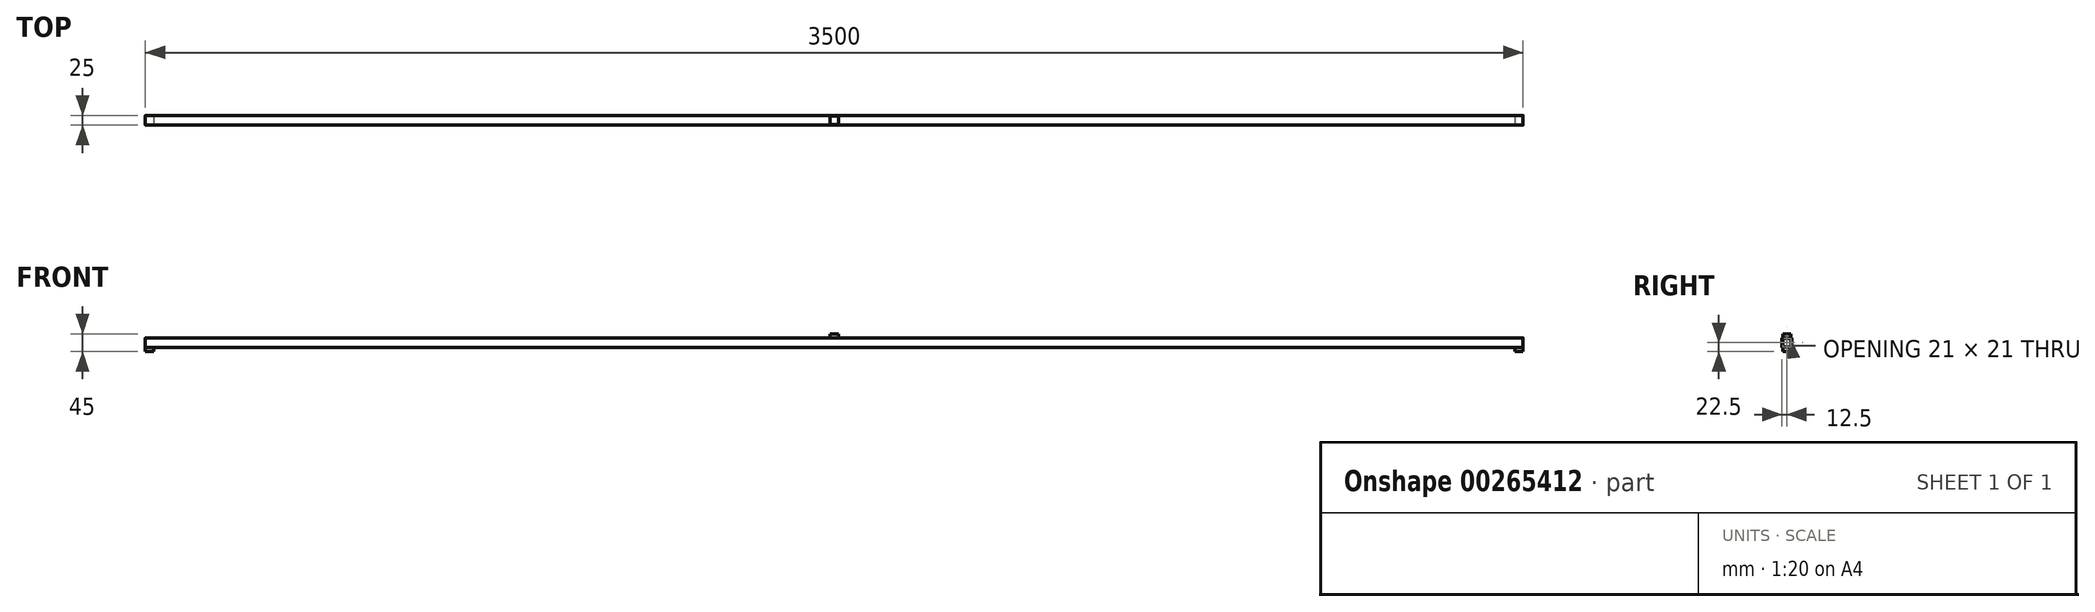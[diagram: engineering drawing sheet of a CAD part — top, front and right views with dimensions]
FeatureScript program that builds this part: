
annotation { "Feature Type Name" : "Feature", "Feature Type Description" : "" }
export const myFeature = defineFeature(function(context is Context, id is Id, definition is map)
    precondition{}
    {
        {
            var Q0;
            Q0=qCreatedBy(makeId("Right.planeOp"),FACE);
            var sketch = newSketch(context, id + "F0", { "sketchPlane" : qUnion([Q0])});
            skLineSegment(sketch, "E0.bottom", {"start": v(10.5, 12.5) * mm, "end": v(-10.5, 12.5) * mm});
            skLineSegment(sketch, "E0.top", {"start": v(10.5, -12.5) * mm, "end": v(-10.5, -12.5) * mm});
            skLineSegment(sketch, "E0.left", {"start": v(12.5, 10.5) * mm, "end": v(12.5, -10.5) * mm});
            skLineSegment(sketch, "E0.right", {"start": v(-12.5, 10.5) * mm, "end": v(-12.5, -10.5) * mm});
            skPoint(sketch, "E0.middle", {"position": v(0, 0) * mm});
            skLineSegment(sketch, "E1.bottom", {"start": v(8.5, 10.5) * mm, "end": v(-8.5, 10.5) * mm});
            skLineSegment(sketch, "E1.top", {"start": v(8.5, -10.5) * mm, "end": v(-8.5, -10.5) * mm});
            skLineSegment(sketch, "E1.left", {"start": v(10.5, 8.5) * mm, "end": v(10.5, -8.5) * mm});
            skLineSegment(sketch, "E1.right", {"start": v(-10.5, 8.5) * mm, "end": v(-10.5, -8.5) * mm});
            skPoint(sketch, "E2.visualSharp", {"position": v(12.5, 12.5) * mm});
            skArc(sketch, "E2.filletArc", {"start": v(12.5, 10.5) * mm, "mid": v(11.91, 11.91) * mm, "end": v(10.5, 12.5) * mm});
            skPoint(sketch, "E3.visualSharp", {"position": v(-12.5, 12.5) * mm});
            skArc(sketch, "E3.filletArc", {"start": v(-10.5, 12.5) * mm, "mid": v(-11.91, 11.91) * mm, "end": v(-12.5, 10.5) * mm});
            skArc(sketch, "E4.filletArc", {"start": v(-8.5, 10.5) * mm, "mid": v(-9.91, 9.91) * mm, "end": v(-10.5, 8.5) * mm});
            skArc(sketch, "E5.filletArc", {"start": v(10.5, 8.5) * mm, "mid": v(9.91, 9.91) * mm, "end": v(8.5, 10.5) * mm});
            skPoint(sketch, "E6.visualSharp", {"position": v(12.5, -12.5) * mm});
            skArc(sketch, "E6.filletArc", {"start": v(10.5, -12.5) * mm, "mid": v(11.91, -11.91) * mm, "end": v(12.5, -10.5) * mm});
            skArc(sketch, "E7.filletArc", {"start": v(8.5, -10.5) * mm, "mid": v(9.91, -9.91) * mm, "end": v(10.5, -8.5) * mm});
            skPoint(sketch, "E8.visualSharp", {"position": v(-10.5, -10.5) * mm});
            skArc(sketch, "E8.filletArc", {"start": v(-10.5, -8.5) * mm, "mid": v(-9.91, -9.91) * mm, "end": v(-8.5, -10.5) * mm});
            skPoint(sketch, "E9.visualSharp", {"position": v(-12.5, -12.5) * mm});
            skArc(sketch, "E9.filletArc", {"start": v(-12.5, -10.5) * mm, "mid": v(-11.91, -11.91) * mm, "end": v(-10.5, -12.5) * mm});
            skSolve(sketch);
        }
        {
            var Q0;
            Q0 = qSketchRegion(id + "F0", true);
            var Q1;
            Q1=makeQuery(id+"F0.imprint","IMPRINT",FACE,{"disambiguationData":[TD([[makeQuery(id+"F0.imprint","IMPRINT",EDGE,{"derivedFrom":sQuery(id+"F0.wireOp",EDGE,"E0.bottom")}),1.0]])]});
            extrude(context, id + "F1", {"entities" : qUnion([Q0, Q1]), "endBound" : BoundingType.SYMMETRIC, "depth" : 3500 * mm});
        }
        {
            var Q0;
            Q0=makeQuery(id+"F1.opExtrude","SWEPT_FACE",FACE,{"disambiguationData":[OSD([sQuery(id+"F0.wireOp",EDGE,"E0.bottom")])]});
            var sketch = newSketch(context, id + "F2", { "sketchPlane" : qUnion([Q0])});
            skLineSegment(sketch, "E10.bottom", {"start": v(10.46, 10.5) * mm, "end": v(-10.46, 10.5) * mm});
            skLineSegment(sketch, "E10.top", {"start": v(10.46, -10.5) * mm, "end": v(-10.46, -10.5) * mm});
            skLineSegment(sketch, "E10.left", {"start": v(10.46, 10.5) * mm, "end": v(10.46, -10.5) * mm});
            skLineSegment(sketch, "E10.right", {"start": v(-10.46, 10.5) * mm, "end": v(-10.46, -10.5) * mm});
            skPoint(sketch, "E10.middle", {"position": v(0, 0) * mm});
            skSolve(sketch);
        }
        {
            var Q0;
            Q0 = qSketchRegion(id + "F2", true);
            extrude(context, id + "F3", {"entities" : qUnion([Q0]), "operationType" : NewBodyOperationType.ADD, "depth" : 10 * mm});
        }
        {
            var Q0;
            Q0=makeQuery(id+"F1.opExtrude","SWEPT_FACE",FACE,{"disambiguationData":[OSD([sQuery(id+"F0.wireOp",EDGE,"E0.top")])]});
            var sketch = newSketch(context, id + "F4", { "sketchPlane" : qUnion([Q0])});
            skLineSegment(sketch, "E11.bottom", {"start": v(-1750, -10.5) * mm, "end": v(-1728.66, -10.5) * mm});
            skLineSegment(sketch, "E11.top", {"start": v(-1750, 10.5) * mm, "end": v(-1728.66, 10.5) * mm});
            skLineSegment(sketch, "E11.left", {"start": v(-1750, -10.5) * mm, "end": v(-1750, 10.5) * mm});
            skLineSegment(sketch, "E11.right", {"start": v(-1728.66, -10.5) * mm, "end": v(-1728.66, 10.5) * mm});
            skLineSegment(sketch, "E12.bottom", {"start": v(1750, -10.5) * mm, "end": v(1729.28, -10.5) * mm});
            skLineSegment(sketch, "E12.top", {"start": v(1750, 10.5) * mm, "end": v(1729.28, 10.5) * mm});
            skLineSegment(sketch, "E12.left", {"start": v(1750, -10.5) * mm, "end": v(1750, 10.5) * mm});
            skLineSegment(sketch, "E12.right", {"start": v(1729.28, -10.5) * mm, "end": v(1729.28, 10.5) * mm});
            skSolve(sketch);
        }
        {
            var Q0;
            Q0=makeQuery(id+"F4.imprint","IMPRINT",FACE,{"disambiguationData":[TD([[makeQuery(id+"F4.imprint","IMPRINT",EDGE,{"derivedFrom":sQuery(id+"F4.wireOp",EDGE,"E11.bottom")}),-1.0]])]});
            extrude(context, id + "F5", {"entities" : qUnion([Q0]), "operationType" : NewBodyOperationType.ADD, "depth" : 10 * mm});
        }
        {
            var Q0;
            Q0=makeQuery(id+"F4.imprint","IMPRINT",FACE,{"disambiguationData":[TD([[makeQuery(id+"F4.imprint","IMPRINT",EDGE,{"derivedFrom":sQuery(id+"F4.wireOp",EDGE,"E12.bottom")}),-1.0]])]});
            extrude(context, id + "F6", {"entities" : qUnion([Q0]), "operationType" : NewBodyOperationType.ADD, "depth" : 10 * mm});
        }
    });
